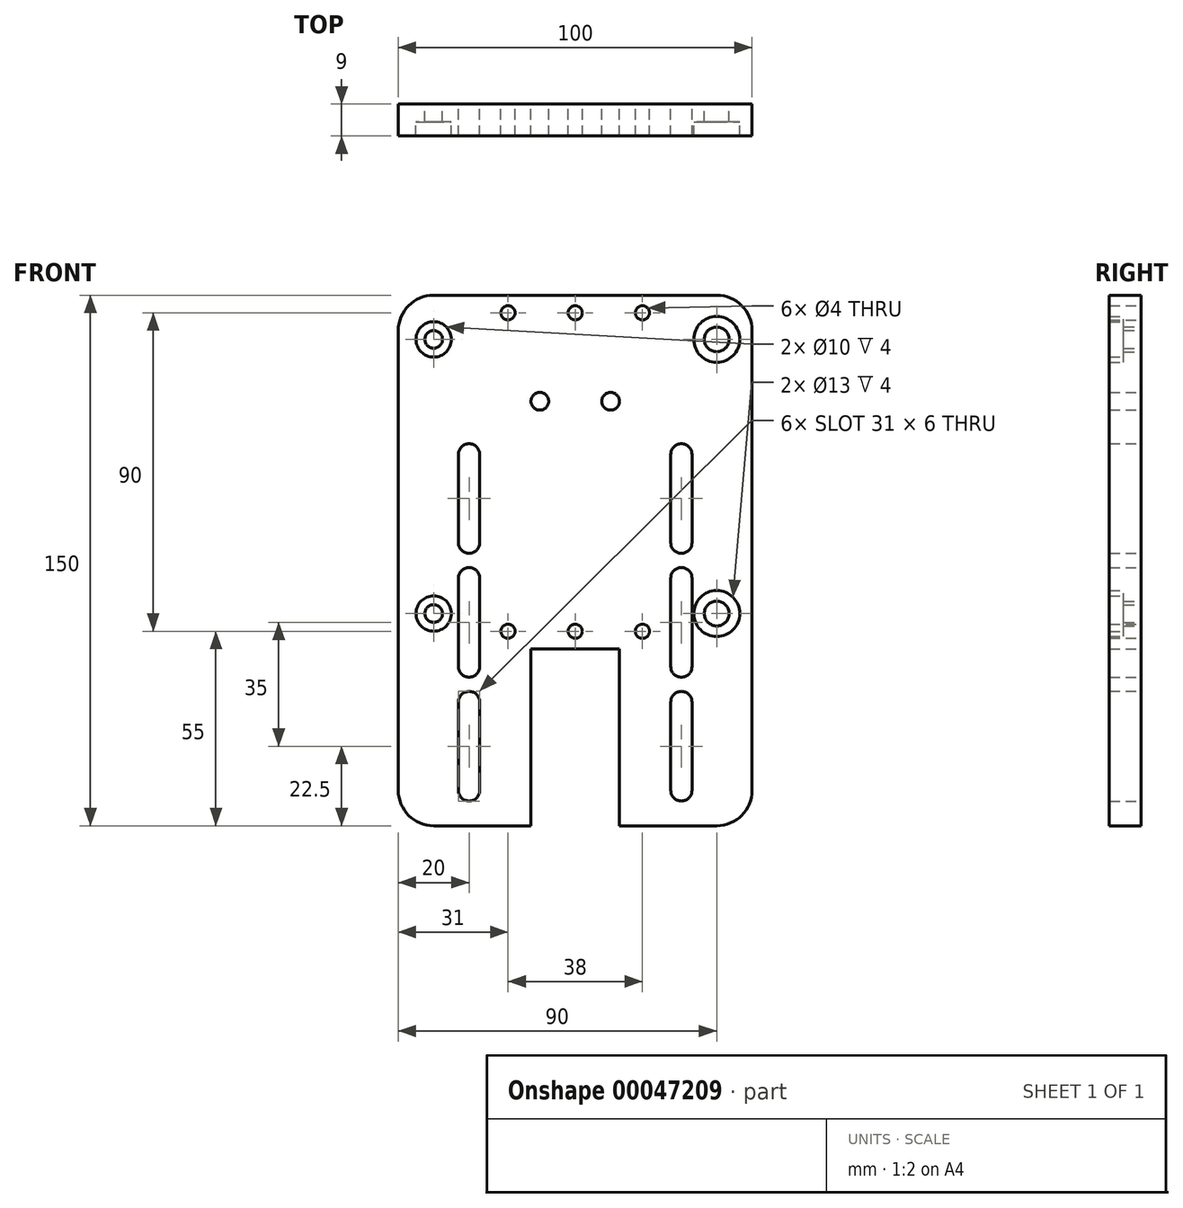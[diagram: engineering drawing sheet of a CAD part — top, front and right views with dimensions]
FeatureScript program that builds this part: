
annotation { "Feature Type Name" : "Feature", "Feature Type Description" : "" }
export const myFeature = defineFeature(function(context is Context, id is Id, definition is map)
    precondition{}
    {
        {
            var Q0;
            Q0=qCreatedBy(makeId("Front.planeOp"),FACE);
            var sketch = newSketch(context, id + "F0", { "sketchPlane" : qUnion([Q0])});
            skLineSegment(sketch, "E0.bottom", {"start": v(-40, 150) * mm, "end": v(40, 150) * mm});
            skLineSegment(sketch, "E0.top", {"start": v(-40, 0) * mm, "end": v(-12.5, 0) * mm});
            skLineSegment(sketch, "E0.left", {"start": v(-50, 140) * mm, "end": v(-50, 10) * mm});
            skLineSegment(sketch, "E0.right", {"start": v(50, 140) * mm, "end": v(50, 10) * mm});
            skCircle(sketch, "E1", {"center": v(-40, 137.5) * mm, "radius": 2.5 * mm});
            skCircle(sketch, "E2", {"center": v(-40, 60) * mm, "radius": 2.5 * mm});
            skCircle(sketch, "E3", {"center": v(40, 137.5) * mm, "radius": 3.5 * mm});
            skCircle(sketch, "E4", {"center": v(40, 60) * mm, "radius": 3.5 * mm});
            skPoint(sketch, "E5.visualSharp", {"position": v(-50, 150) * mm});
            skArc(sketch, "E5.filletArc", {"start": v(-40, 150) * mm, "mid": v(-47.07, 147.07) * mm, "end": v(-50, 140) * mm});
            skPoint(sketch, "E6.visualSharp", {"position": v(50, 150) * mm});
            skArc(sketch, "E6.filletArc", {"start": v(50, 140) * mm, "mid": v(47.07, 147.07) * mm, "end": v(40, 150) * mm});
            skPoint(sketch, "E7.visualSharp", {"position": v(50, 0) * mm});
            skArc(sketch, "E7.filletArc", {"start": v(40, 0) * mm, "mid": v(47.07, 2.93) * mm, "end": v(50, 10) * mm});
            skPoint(sketch, "E8.visualSharp", {"position": v(-50, 0) * mm});
            skArc(sketch, "E8.filletArc", {"start": v(-50, 10) * mm, "mid": v(-47.07, 2.93) * mm, "end": v(-40, 0) * mm});
            skCircle(sketch, "E9", {"center": v(-10, 120) * mm, "radius": 2.5 * mm});
            skCircle(sketch, "E10", {"center": v(10, 120) * mm, "radius": 2.5 * mm});
            skCircle(sketch, "E11", {"center": v(0, 145) * mm, "radius": 2 * mm});
            skCircle(sketch, "E12", {"center": v(-19, 145) * mm, "radius": 2 * mm});
            skCircle(sketch, "E13.MirrorC", {"center": v(19, 145) * mm, "radius": 2 * mm});
            skCircle(sketch, "E14", {"center": v(0, 55) * mm, "radius": 2 * mm});
            skCircle(sketch, "E15", {"center": v(-19, 55) * mm, "radius": 2 * mm});
            skCircle(sketch, "E16.MirrorC", {"center": v(19, 55) * mm, "radius": 2 * mm});
            skArc(sketch, "E17", {"start": v(-33, 10) * mm, "mid": v(-30, 7) * mm, "end": v(-27, 10) * mm});
            skArc(sketch, "E18", {"start": v(-27, 35) * mm, "mid": v(-30, 38) * mm, "end": v(-33, 35) * mm});
            skLineSegment(sketch, "E19", {"start": v(-33, 10) * mm, "end": v(-33, 35) * mm});
            skLineSegment(sketch, "E20", {"start": v(-27, 35) * mm, "end": v(-27, 10) * mm});
            skArc(sketch, "E21.MirrorCS", {"start": v(27, 35) * mm, "mid": v(30, 38) * mm, "end": v(33, 35) * mm});
            skLineSegment(sketch, "E22.MirrorCS", {"start": v(33, 10) * mm, "end": v(33, 35) * mm});
            skLineSegment(sketch, "E23.MirrorCS", {"start": v(27, 35) * mm, "end": v(27, 10) * mm});
            skArc(sketch, "E24.MirrorCS", {"start": v(33, 10) * mm, "mid": v(30, 7) * mm, "end": v(27, 10) * mm});
            skLineSegment(sketch, "E25", {"start": v(-43.34, 40) * mm, "end": v(40.76, 40) * mm, "construction": true});
            skLineSegment(sketch, "E26.MirrorCS", {"start": v(-33, 70) * mm, "end": v(-33, 45) * mm});
            skArc(sketch, "E27.MirrorCS", {"start": v(-27, 45) * mm, "mid": v(-30, 42) * mm, "end": v(-33, 45) * mm});
            skArc(sketch, "E28.MirrorCS", {"start": v(-33, 70) * mm, "mid": v(-30, 73) * mm, "end": v(-27, 70) * mm});
            skLineSegment(sketch, "E29.MirrorCS", {"start": v(-27, 45) * mm, "end": v(-27, 70) * mm});
            skLineSegment(sketch, "E30.MirrorCS", {"start": v(33, 70) * mm, "end": v(33, 45) * mm});
            skLineSegment(sketch, "E31.MirrorCS", {"start": v(27, 45) * mm, "end": v(27, 70) * mm});
            skArc(sketch, "E32.MirrorCS", {"start": v(27, 45) * mm, "mid": v(30, 42) * mm, "end": v(33, 45) * mm});
            skArc(sketch, "E33.MirrorCS", {"start": v(33, 70) * mm, "mid": v(30, 73) * mm, "end": v(27, 70) * mm});
            skLineSegment(sketch, "E34", {"start": v(-42.95, 75) * mm, "end": v(41.23, 75) * mm, "construction": true});
            skLineSegment(sketch, "E35.MirrorCS", {"start": v(-33, 80) * mm, "end": v(-33, 105) * mm});
            skLineSegment(sketch, "E36.MirrorCS", {"start": v(-27, 105) * mm, "end": v(-27, 80) * mm});
            skArc(sketch, "E37.MirrorCS", {"start": v(-27, 105) * mm, "mid": v(-30, 108) * mm, "end": v(-33, 105) * mm});
            skArc(sketch, "E38.MirrorCS", {"start": v(-33, 80) * mm, "mid": v(-30, 77) * mm, "end": v(-27, 80) * mm});
            skLineSegment(sketch, "E39.MirrorCS", {"start": v(33, 80) * mm, "end": v(33, 105) * mm});
            skArc(sketch, "E40.MirrorCS", {"start": v(33, 80) * mm, "mid": v(30, 77) * mm, "end": v(27, 80) * mm});
            skLineSegment(sketch, "E41.MirrorCS", {"start": v(27, 105) * mm, "end": v(27, 80) * mm});
            skArc(sketch, "E42.MirrorCS", {"start": v(27, 105) * mm, "mid": v(30, 108) * mm, "end": v(33, 105) * mm});
            skLineSegment(sketch, "E43", {"start": v(-12.5, 0) * mm, "end": v(-12.5, 50) * mm});
            skLineSegment(sketch, "E44", {"start": v(-12.5, 50) * mm, "end": v(0, 50) * mm});
            skLineSegment(sketch, "E45.MirrorCS", {"start": v(12.5, 0) * mm, "end": v(12.5, 50) * mm});
            skLineSegment(sketch, "E46.MirrorCS", {"start": v(12.5, 50) * mm, "end": v(0, 50) * mm});
            skLineSegment(sketch, "E47.trimOffspring", {"start": v(12.5, 0) * mm, "end": v(40, 0) * mm});
            skCircle(sketch, "E48", {"center": v(-40, 137.5) * mm, "radius": 5 * mm});
            skCircle(sketch, "E49", {"center": v(-40, 60) * mm, "radius": 5 * mm});
            skCircle(sketch, "E50", {"center": v(40, 137.5) * mm, "radius": 6.5 * mm});
            skCircle(sketch, "E51", {"center": v(40, 60) * mm, "radius": 6.5 * mm});
            skSolve(sketch);
        }
        {
            var Q0;
            Q0=makeQuery(id+"F0.imprint","IMPRINT",FACE,{"disambiguationData":[TD([[makeQuery(id+"F0.imprint","IMPRINT",EDGE,{"derivedFrom":sQuery(id+"F0.wireOp",EDGE,"E0.bottom")}),-1.0]])]});
            extrude(context, id + "F1", {"entities" : qUnion([Q0]), "depth" : 9 * mm});
        }
        {
            var Q0;
            Q0=makeQuery(id+"F0.imprint","IMPRINT",FACE,{"disambiguationData":[TD([[makeQuery(id+"F0.imprint","IMPRINT",EDGE,{"derivedFrom":sQuery(id+"F0.wireOp",EDGE,"E1")}),-1.0]])]});
            var Q1;
            Q1=makeQuery(id+"F0.imprint","IMPRINT",FACE,{"disambiguationData":[TD([[makeQuery(id+"F0.imprint","IMPRINT",EDGE,{"derivedFrom":sQuery(id+"F0.wireOp",EDGE,"E3")}),-1.0]])]});
            var Q2;
            Q2=makeQuery(id+"F0.imprint","IMPRINT",FACE,{"disambiguationData":[TD([[makeQuery(id+"F0.imprint","IMPRINT",EDGE,{"derivedFrom":sQuery(id+"F0.wireOp",EDGE,"E4")}),-1.0]])]});
            var Q3;
            Q3=makeQuery(id+"F0.imprint","IMPRINT",FACE,{"disambiguationData":[TD([[makeQuery(id+"F0.imprint","IMPRINT",EDGE,{"derivedFrom":sQuery(id+"F0.wireOp",EDGE,"E2")}),-1.0]])]});
            extrude(context, id + "F2", {"entities" : qUnion([Q0, Q1, Q2, Q3]), "operationType" : NewBodyOperationType.ADD, "depth" : 5 * mm});
        }
    });
